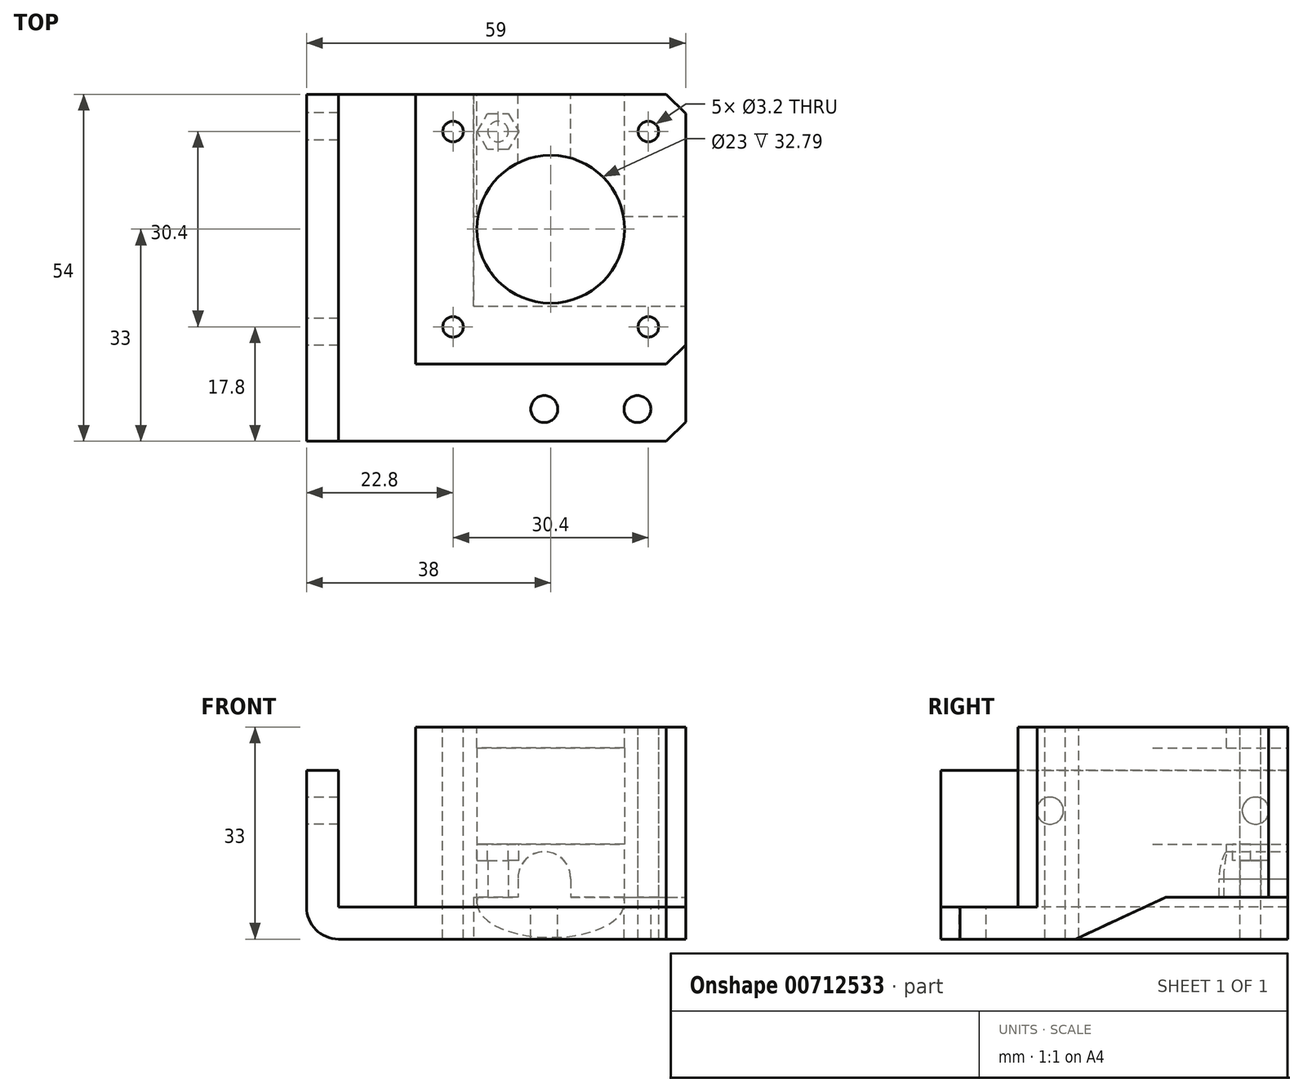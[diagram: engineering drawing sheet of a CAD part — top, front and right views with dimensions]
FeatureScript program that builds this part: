
annotation { "Feature Type Name" : "Feature", "Feature Type Description" : "" }
export const myFeature = defineFeature(function(context is Context, id is Id, definition is map)
    precondition{}
    {
        {
            var Q0;
            Q0=qCreatedBy(makeId("Top.planeOp"),FACE);
            var sketch = newSketch(context, id + "F0", { "sketchPlane" : qUnion([Q0])});
            skLineSegment(sketch, "E0.bottom", {"start": v(0, 0) * mm, "end": v(59, 0) * mm});
            skLineSegment(sketch, "E0.top", {"start": v(0, 54) * mm, "end": v(59, 54) * mm});
            skLineSegment(sketch, "E0.left", {"start": v(0, 0) * mm, "end": v(0, 54) * mm});
            skLineSegment(sketch, "E0.right", {"start": v(59, 0) * mm, "end": v(59, 54) * mm});
            skSolve(sketch);
        }
        {
            var Q0;
            Q0=makeQuery(id+"F0.imprint","IMPRINT",FACE,{"disambiguationData":[TD([[makeQuery(id+"F0.imprint","IMPRINT",EDGE,{"derivedFrom":sQuery(id+"F0.wireOp",EDGE,"E0.bottom")}),1.0]])]});
            extrude(context, id + "F1", {"entities" : qUnion([Q0]), "depth" : 5 * mm, "offsetDistance" : 25 * mm});
        }
        {
            var Q0;
            Q0=makeQuery(id+"F1.opExtrude","CAP_FACE",FACE,{"disambiguationData":[OSD([sQuery(id+"F0.wireOp",EDGE,"E0.bottom"),sQuery(id+"F0.wireOp",EDGE,"E0.top"),sQuery(id+"F0.wireOp",EDGE,"E0.left"),sQuery(id+"F0.wireOp",EDGE,"E0.right")])],"isStart":false});
            var sketch = newSketch(context, id + "F2", { "sketchPlane" : qUnion([Q0])});
            skLineSegment(sketch, "E1.bottom", {"start": v(0, 54) * mm, "end": v(5, 54) * mm});
            skLineSegment(sketch, "E1.top", {"start": v(0, 0) * mm, "end": v(5, 0) * mm});
            skLineSegment(sketch, "E1.left", {"start": v(0, 54) * mm, "end": v(0, 0) * mm});
            skLineSegment(sketch, "E1.right", {"start": v(5, 54) * mm, "end": v(5, 0) * mm});
            skSolve(sketch);
        }
        {
            var Q0;
            Q0=makeQuery(id+"F2.imprint","IMPRINT",FACE,{"disambiguationData":[TD([[makeQuery(id+"F2.imprint","IMPRINT",EDGE,{"derivedFrom":sQuery(id+"F2.wireOp",EDGE,"E1.bottom")}),-1.0]])]});
            extrude(context, id + "F3", {"entities" : qUnion([Q0]), "operationType" : NewBodyOperationType.ADD, "depth" : 21.25 * mm, "offsetDistance" : 25 * mm});
        }
        {
            var Q0;
            Q0=makeQuery(id+"F1.opExtrude","CAP_FACE",FACE,{"disambiguationData":[OSD([sQuery(id+"F0.wireOp",EDGE,"E0.bottom"),sQuery(id+"F0.wireOp",EDGE,"E0.top"),sQuery(id+"F0.wireOp",EDGE,"E0.left"),sQuery(id+"F0.wireOp",EDGE,"E0.right")])],"isStart":false});
            var sketch = newSketch(context, id + "F4", { "sketchPlane" : qUnion([Q0])});
            skLineSegment(sketch, "E2.bottom", {"start": v(59, 54) * mm, "end": v(17, 54) * mm});
            skLineSegment(sketch, "E2.top", {"start": v(59, 12) * mm, "end": v(17, 12) * mm});
            skLineSegment(sketch, "E2.left", {"start": v(59, 54) * mm, "end": v(59, 12) * mm});
            skLineSegment(sketch, "E2.right", {"start": v(17, 54) * mm, "end": v(17, 12) * mm});
            skSolve(sketch);
        }
        {
            var Q0;
            Q0=makeQuery(id+"F4.imprint","IMPRINT",FACE,{"disambiguationData":[TD([[makeQuery(id+"F4.imprint","IMPRINT",EDGE,{"derivedFrom":sQuery(id+"F4.wireOp",EDGE,"E2.bottom")}),-1.0]])]});
            extrude(context, id + "F5", {"entities" : qUnion([Q0]), "operationType" : NewBodyOperationType.ADD, "depth" : 28 * mm, "offsetDistance" : 25 * mm});
        }
        {
            var Q0;
            Q0=makeQuery(id+"F5.opExtrude","CAP_FACE",FACE,{"disambiguationData":[OSD([sQuery(id+"F4.wireOp",EDGE,"E2.bottom"),sQuery(id+"F4.wireOp",EDGE,"E2.top"),sQuery(id+"F4.wireOp",EDGE,"E2.left"),sQuery(id+"F4.wireOp",EDGE,"E2.right")])],"isStart":false});
            var sketch = newSketch(context, id + "F6", { "sketchPlane" : qUnion([Q0])});
            skCircle(sketch, "E3", {"center": v(38, 33) * mm, "radius": 11.5 * mm});
            skCircle(sketch, "E4", {"center": v(22.8, 48.2) * mm, "radius": 1.6 * mm});
            skCircle(sketch, "E5", {"center": v(53.2, 48.2) * mm, "radius": 1.6 * mm});
            skCircle(sketch, "E6", {"center": v(22.8, 17.8) * mm, "radius": 1.6 * mm});
            skCircle(sketch, "E7", {"center": v(53.2, 17.8) * mm, "radius": 1.6 * mm});
            skSolve(sketch);
        }
        {
            var Q0;
            Q0=makeQuery(id+"F6.imprint","IMPRINT",FACE,{"disambiguationData":[TD([[makeQuery(id+"F6.imprint","IMPRINT",EDGE,{"derivedFrom":sQuery(id+"F6.wireOp",EDGE,"E4")}),1.0]])]});
            var Q1;
            Q1=makeQuery(id+"F6.imprint","IMPRINT",FACE,{"disambiguationData":[TD([[makeQuery(id+"F6.imprint","IMPRINT",EDGE,{"derivedFrom":sQuery(id+"F6.wireOp",EDGE,"E3")}),1.0]])]});
            var Q2;
            Q2=makeQuery(id+"F6.imprint","IMPRINT",FACE,{"disambiguationData":[TD([[makeQuery(id+"F6.imprint","IMPRINT",EDGE,{"derivedFrom":sQuery(id+"F6.wireOp",EDGE,"E5")}),1.0]])]});
            var Q3;
            Q3=makeQuery(id+"F6.imprint","IMPRINT",FACE,{"disambiguationData":[TD([[makeQuery(id+"F6.imprint","IMPRINT",EDGE,{"derivedFrom":sQuery(id+"F6.wireOp",EDGE,"E6")}),1.0]])]});
            var Q4;
            Q4=makeQuery(id+"F6.imprint","IMPRINT",FACE,{"disambiguationData":[TD([[makeQuery(id+"F6.imprint","IMPRINT",EDGE,{"derivedFrom":sQuery(id+"F6.wireOp",EDGE,"E7")}),1.0]])]});
            extrude(context, id + "F7", {"entities" : qUnion([Q0, Q1, Q2, Q3, Q4]), "operationType" : NewBodyOperationType.REMOVE, "endBound" : BoundingType.THROUGH_ALL, "oppositeDirection" : true, "depth" : 25 * mm, "offsetDistance" : 25 * mm});
        }
        {
            var Q0;
            Q0=makeQuery(id+"F1.opExtrude","CAP_FACE",FACE,{"disambiguationData":[OSD([sQuery(id+"F0.wireOp",EDGE,"E0.bottom"),sQuery(id+"F0.wireOp",EDGE,"E0.top"),sQuery(id+"F0.wireOp",EDGE,"E0.left"),sQuery(id+"F0.wireOp",EDGE,"E0.right")])],"isStart":false});
            var sketch = newSketch(context, id + "F8", { "sketchPlane" : qUnion([Q0])});
            skCircle(sketch, "E8", {"center": v(37, 5) * mm, "radius": 2.1 * mm});
            skCircle(sketch, "E9", {"center": v(51.5, 5) * mm, "radius": 2.1 * mm});
            skSolve(sketch);
        }
        {
            var Q0;
            Q0=makeQuery(id+"F8.imprint","IMPRINT",FACE,{"disambiguationData":[TD([[makeQuery(id+"F8.imprint","IMPRINT",EDGE,{"derivedFrom":sQuery(id+"F8.wireOp",EDGE,"E8")}),1.0]])]});
            var Q1;
            Q1=makeQuery(id+"F8.imprint","IMPRINT",FACE,{"disambiguationData":[TD([[makeQuery(id+"F8.imprint","IMPRINT",EDGE,{"derivedFrom":sQuery(id+"F8.wireOp",EDGE,"E9")}),1.0]])]});
            extrude(context, id + "F9", {"entities" : qUnion([Q0, Q1]), "operationType" : NewBodyOperationType.REMOVE, "endBound" : BoundingType.THROUGH_ALL, "oppositeDirection" : true, "depth" : 25 * mm, "offsetDistance" : 25 * mm});
        }
        {
            var Q0;
            Q0=makeQuery(id+"F5.boolean.opBoolean","MERGE",FACE,{"derivedFrom":[makeQuery(id+"F3.boolean.opBoolean","MERGE",FACE,{"derivedFrom":[makeQuery(id+"F1.opExtrude","SWEPT_FACE",FACE,{"disambiguationData":[OSD([sQuery(id+"F0.wireOp",EDGE,"E0.top")])]}),makeQuery(id+"F3.opExtrude","SWEPT_FACE",FACE,{"disambiguationData":[OSD([sQuery(id+"F2.wireOp",EDGE,"E1.bottom")])]})]}),makeQuery(id+"F5.opExtrude","SWEPT_FACE",FACE,{"disambiguationData":[OSD([sQuery(id+"F4.wireOp",EDGE,"E2.bottom")])]})]});
            var sketch = newSketch(context, id + "F10", { "sketchPlane" : qUnion([Q0])});
            skLineSegment(sketch, "E10.bottom", {"start": v(-49.5, 29.75) * mm, "end": v(-26.5, 29.75) * mm});
            skLineSegment(sketch, "E10.top", {"start": v(-49.5, 14.75) * mm, "end": v(-26.5, 14.75) * mm});
            skLineSegment(sketch, "E10.left", {"start": v(-49.5, 29.75) * mm, "end": v(-49.5, 14.75) * mm});
            skLineSegment(sketch, "E10.right", {"start": v(-26.5, 29.75) * mm, "end": v(-26.5, 14.75) * mm});
            skSolve(sketch);
        }
        {
            var Q0;
            Q0=makeQuery(id+"F10.imprint","IMPRINT",FACE,{"disambiguationData":[TD([[makeQuery(id+"F10.imprint","IMPRINT",EDGE,{"derivedFrom":sQuery(id+"F10.wireOp",EDGE,"E10.bottom")}),-1.0]])]});
            extrude(context, id + "F11", {"entities" : qUnion([Q0]), "operationType" : NewBodyOperationType.REMOVE, "endBound" : BoundingType.UP_TO_NEXT, "oppositeDirection" : true, "depth" : 25 * mm, "offsetDistance" : 25 * mm});
        }
        {
            var Q0;
            Q0=makeQuery(id+"F5.boolean.opBoolean","MERGE",FACE,{"derivedFrom":[makeQuery(id+"F1.opExtrude","SWEPT_FACE",FACE,{"disambiguationData":[OSD([sQuery(id+"F0.wireOp",EDGE,"E0.right")])]}),makeQuery(id+"F5.opExtrude","SWEPT_FACE",FACE,{"disambiguationData":[OSD([sQuery(id+"F4.wireOp",EDGE,"E2.left")])]})]});
            var sketch = newSketch(context, id + "F12", { "sketchPlane" : qUnion([Q0])});
            skLineSegment(sketch, "E11", {"start": v(54, 6.5) * mm, "end": v(35, 6.5) * mm});
            skLineSegment(sketch, "E12", {"start": v(35, 6.5) * mm, "end": v(21, 0) * mm});
            skLineSegment(sketch, "E13", {"start": v(21, 0) * mm, "end": v(54, 0) * mm});
            skLineSegment(sketch, "E14", {"start": v(54, 0) * mm, "end": v(54, 6.5) * mm});
            skSolve(sketch);
        }
        {
            var Q0;
            Q0=makeQuery(id+"F12.imprint","IMPRINT",FACE,{"disambiguationData":[TD([[makeQuery(id+"F12.imprint","IMPRINT",EDGE,{"derivedFrom":sQuery(id+"F12.wireOp",EDGE,"E11")}),1.0]])]});
            extrude(context, id + "F13", {"entities" : qUnion([Q0]), "operationType" : NewBodyOperationType.REMOVE, "oppositeDirection" : true, "depth" : 33 * mm, "offsetDistance" : 25 * mm});
        }
        {
            var Q0;
            Q0=makeQuery(id+"F1.opExtrude","SWEPT_EDGE",EDGE,{"disambiguationData":[OSD([sQuery(id+"F0.wireOp",EDGE,"E0.bottom"),sQuery(id+"F0.wireOp",EDGE,"E0.right")])]});
            var Q1;
            Q1=makeQuery(id+"F5.opExtrude","SWEPT_EDGE",EDGE,{"disambiguationData":[OSD([sQuery(id+"F0.wireOp",EDGE,"E0.right"),sQuery(id+"F4.wireOp",EDGE,"E2.top"),sQuery(id+"F4.wireOp",EDGE,"E2.left")])]});
            var Q2;
            Q2=makeQuery(id+"F5.boolean.opBoolean","MERGE",EDGE,{"derivedFrom":[makeQuery(id+"F1.opExtrude","SWEPT_EDGE",EDGE,{"disambiguationData":[OSD([sQuery(id+"F0.wireOp",EDGE,"E0.top"),sQuery(id+"F0.wireOp",EDGE,"E0.right")])]}),makeQuery(id+"F5.opExtrude","SWEPT_EDGE",EDGE,{"disambiguationData":[OSD([sQuery(id+"F4.wireOp",EDGE,"E2.bottom"),sQuery(id+"F4.wireOp",EDGE,"E2.left")])]})]});
            chamfer(context, id + "F14", {"entities" : qUnion([Q0, Q1, Q2]), "width" : 3 * mm, "tangentPropagation" : true});
        }
        {
            var Q0;
            Q0=makeQuery(id+"F5.boolean.opBoolean","MERGE",FACE,{"derivedFrom":[makeQuery(id+"F3.boolean.opBoolean","MERGE",FACE,{"derivedFrom":[makeQuery(id+"F1.opExtrude","SWEPT_FACE",FACE,{"disambiguationData":[OSD([sQuery(id+"F0.wireOp",EDGE,"E0.top")])]}),makeQuery(id+"F3.opExtrude","SWEPT_FACE",FACE,{"disambiguationData":[OSD([sQuery(id+"F2.wireOp",EDGE,"E1.bottom")])]})]}),makeQuery(id+"F5.opExtrude","SWEPT_FACE",FACE,{"disambiguationData":[OSD([sQuery(id+"F4.wireOp",EDGE,"E2.bottom")])]})]});
            var sketch = newSketch(context, id + "F15", { "sketchPlane" : qUnion([Q0])});
            skArc(sketch, "E15", {"start": v(-32.9, 9.39) * mm, "mid": v(-37, 13.6) * mm, "end": v(-41.1, 9.39) * mm});
            skLineSegment(sketch, "E16.bottom", {"start": v(-32.9, 9.39) * mm, "end": v(-32.9, 9.39) * mm});
            skLineSegment(sketch, "E16.top", {"start": v(-41.1, 6.5) * mm, "end": v(-32.9, 6.5) * mm});
            skLineSegment(sketch, "E16.left", {"start": v(-41.1, 9.39) * mm, "end": v(-41.1, 6.5) * mm});
            skLineSegment(sketch, "E16.right", {"start": v(-32.9, 9.39) * mm, "end": v(-32.9, 6.5) * mm});
            skSolve(sketch);
        }
        {
            var Q0;
            Q0=makeQuery(id+"F15.imprint","IMPRINT",FACE,{"disambiguationData":[TD([[makeQuery(id+"F15.imprint","IMPRINT",EDGE,{"derivedFrom":sQuery(id+"F15.wireOp",EDGE,"E15")}),1.0]])]});
            extrude(context, id + "F16", {"entities" : qUnion([Q0]), "operationType" : NewBodyOperationType.REMOVE, "endBound" : BoundingType.UP_TO_NEXT, "oppositeDirection" : true, "depth" : 25 * mm, "offsetDistance" : 25 * mm});
        }
        {
            var Q0;
            Q0=makeQuery(id+"F1.opExtrude","CAP_EDGE",EDGE,{"disambiguationData":[OSD([sQuery(id+"F0.wireOp",EDGE,"E0.left")])],"isStart":true});
            fillet(context, id + "F17", {"entities" : qUnion([Q0]), "radius" : 5 * mm, "tangentPropagation" : true, "allowEdgeOverflow" : false});
        }
        {
            var Q0;
            {var subQ1=sQuery(id+"F12.wireOp",EDGE,"E11");Q0=makeQuery(id+"F16.boolean.opBoolean","SPLIT",FACE,{"disambiguationData":[TD([makeQuery(id+"F16.opExtrude","SWEPT_FACE",FACE,{"disambiguationData":[OSD([sQuery(id+"F15.wireOp",EDGE,"E16.right")])]})])],"derivedFrom":makeQuery(id+"F13.boolean.opBoolean","COPY",FACE,{"derivedFrom":makeQuery(id+"F13.opExtrude","SWEPT_FACE",FACE,{"disambiguationData":[OSD([subQ1])]})})});}
            var sketch = newSketch(context, id + "F18", { "sketchPlane" : qUnion([Q0])});
            skCircle(sketch, "E17", {"center": v(29.8, -48.2) * mm, "radius": 1.6 * mm});
            skSolve(sketch);
        }
        {
            var Q0;
            Q0=makeQuery(id+"F18.imprint","IMPRINT",FACE,{"disambiguationData":[TD([[makeQuery(id+"F18.imprint","IMPRINT",EDGE,{"derivedFrom":sQuery(id+"F18.wireOp",EDGE,"E17")}),1.0]])]});
            extrude(context, id + "F19", {"entities" : qUnion([Q0]), "operationType" : NewBodyOperationType.REMOVE, "endBound" : BoundingType.UP_TO_NEXT, "oppositeDirection" : true, "depth" : 25 * mm, "offsetDistance" : 25 * mm});
        }
        {
            var Q0;
            Q0=makeQuery(id+"F11.boolean.opBoolean","COPY",FACE,{"derivedFrom":makeQuery(id+"F11.opExtrude","SWEPT_FACE",FACE,{"disambiguationData":[OSD([sQuery(id+"F10.wireOp",EDGE,"E10.top")])]})});
            var sketch = newSketch(context, id + "F20", { "sketchPlane" : qUnion([Q0])});
            skCircle(sketch, "E18.cCircle", {"center": v(29.8, 48.2) * mm, "radius": 2.8 * mm, "construction": true});
            skLineSegment(sketch, "E18.0", {"start": v(33.03, 48.2) * mm, "end": v(31.42, 45.4) * mm});
            skLineSegment(sketch, "E18.1", {"start": v(31.42, 45.4) * mm, "end": v(28.18, 45.4) * mm});
            skLineSegment(sketch, "E18.2", {"start": v(28.18, 45.4) * mm, "end": v(26.57, 48.2) * mm});
            skLineSegment(sketch, "E18.3", {"start": v(26.57, 48.2) * mm, "end": v(28.18, 51) * mm});
            skLineSegment(sketch, "E18.4", {"start": v(28.18, 51) * mm, "end": v(31.42, 51) * mm});
            skLineSegment(sketch, "E18.5", {"start": v(31.42, 51) * mm, "end": v(33.03, 48.2) * mm});
            skPoint(sketch, "E18.0.midPoint", {"position": v(32.22, 46.8) * mm});
            skSolve(sketch);
        }
        {
            var Q0;
            Q0=makeQuery(id+"F20.imprint","IMPRINT",FACE,{"disambiguationData":[TD([[makeQuery(id+"F20.imprint","IMPRINT",EDGE,{"derivedFrom":sQuery(id+"F20.wireOp",EDGE,"E18.0")}),-1.0]])]});
            extrude(context, id + "F21", {"entities" : qUnion([Q0]), "operationType" : NewBodyOperationType.REMOVE, "oppositeDirection" : true, "depth" : 2.5 * mm, "offsetDistance" : 25 * mm});
        }
        {
            var Q0;
            Q0=makeQuery(id+"F3.boolean.opBoolean","MERGE",FACE,{"derivedFrom":[makeQuery(id+"F1.opExtrude","SWEPT_FACE",FACE,{"disambiguationData":[OSD([sQuery(id+"F0.wireOp",EDGE,"E0.left")])]}),makeQuery(id+"F3.opExtrude","SWEPT_FACE",FACE,{"disambiguationData":[OSD([sQuery(id+"F2.wireOp",EDGE,"E1.left")])]})]});
            var sketch = newSketch(context, id + "F22", { "sketchPlane" : qUnion([Q0])});
            skCircle(sketch, "E19", {"center": v(-49, 20) * mm, "radius": 2.1 * mm});
            skCircle(sketch, "E20", {"center": v(-17, 20) * mm, "radius": 2.1 * mm});
            skSolve(sketch);
        }
        {
            var Q0;
            Q0=makeQuery(id+"F22.imprint","IMPRINT",FACE,{"disambiguationData":[TD([[makeQuery(id+"F22.imprint","IMPRINT",EDGE,{"derivedFrom":sQuery(id+"F22.wireOp",EDGE,"E19")}),1.0]])]});
            var Q1;
            Q1=makeQuery(id+"F22.imprint","IMPRINT",FACE,{"disambiguationData":[TD([[makeQuery(id+"F22.imprint","IMPRINT",EDGE,{"derivedFrom":sQuery(id+"F22.wireOp",EDGE,"E20")}),1.0]])]});
            extrude(context, id + "F23", {"entities" : qUnion([Q0, Q1]), "operationType" : NewBodyOperationType.REMOVE, "endBound" : BoundingType.UP_TO_NEXT, "oppositeDirection" : true, "depth" : 25 * mm, "offsetDistance" : 25 * mm});
        }
    });
